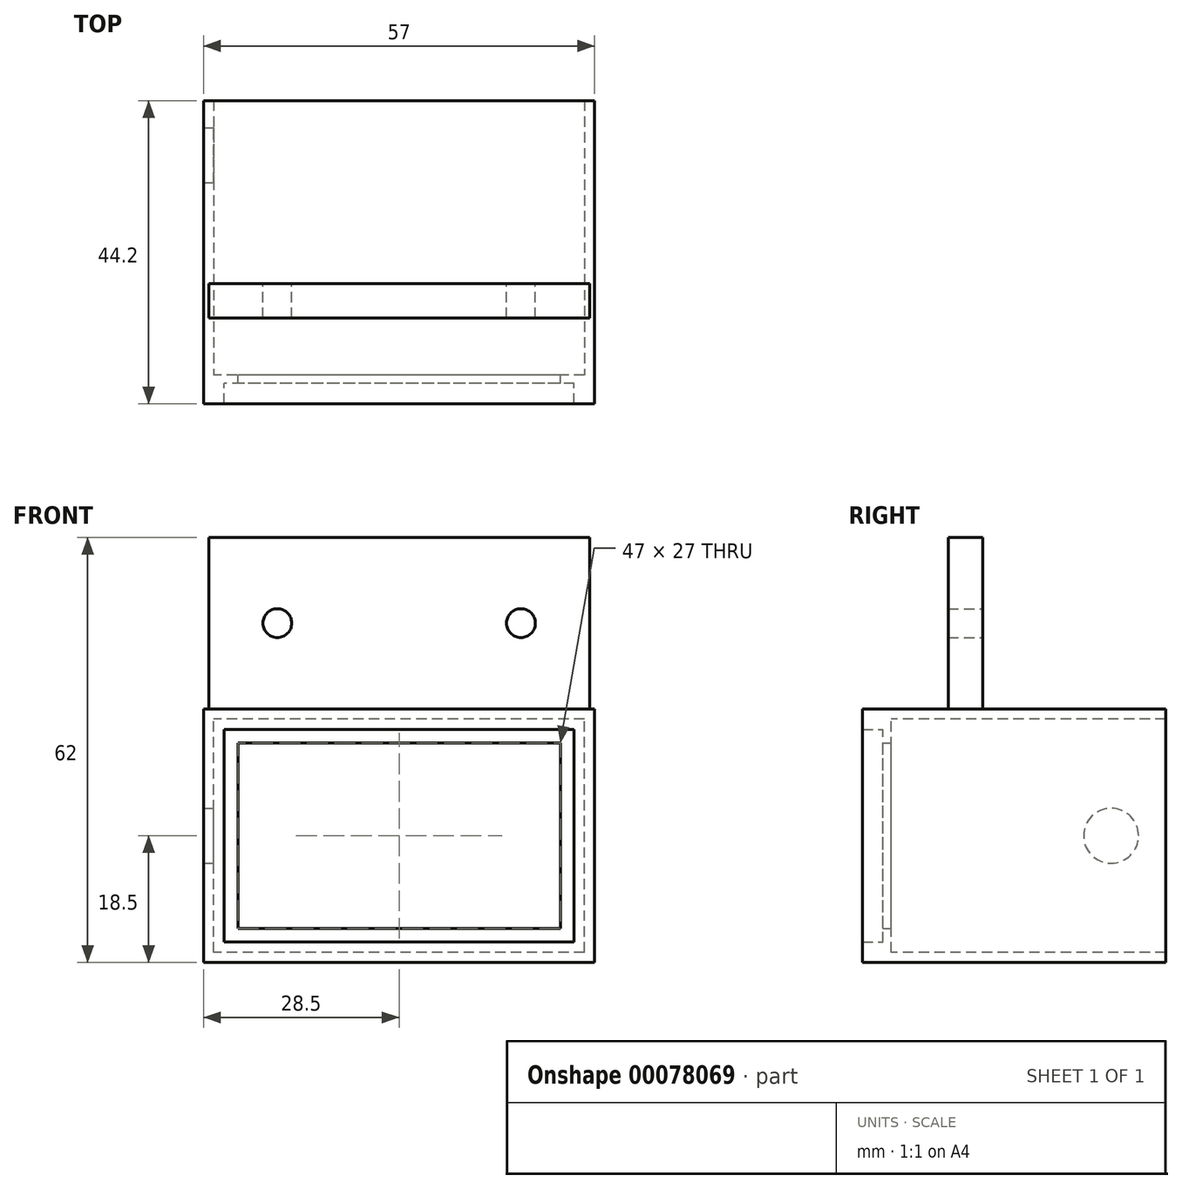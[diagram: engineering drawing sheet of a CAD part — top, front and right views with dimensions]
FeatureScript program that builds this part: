
annotation { "Feature Type Name" : "Feature", "Feature Type Description" : "" }
export const myFeature = defineFeature(function(context is Context, id is Id, definition is map)
    precondition{}
    {
        {
            var Q0;
            Q0=qCreatedBy(makeId("Front.planeOp"),FACE);
            var sketch = newSketch(context, id + "F0", { "sketchPlane" : qUnion([Q0])});
            skLineSegment(sketch, "E0.bottom", {"start": v(23.5, -13.5) * mm, "end": v(-23.5, -13.5) * mm});
            skLineSegment(sketch, "E0.top", {"start": v(23.5, 13.5) * mm, "end": v(-23.5, 13.5) * mm});
            skLineSegment(sketch, "E0.left", {"start": v(23.5, -13.5) * mm, "end": v(23.5, 13.5) * mm});
            skLineSegment(sketch, "E0.right", {"start": v(-23.5, -13.5) * mm, "end": v(-23.5, 13.5) * mm});
            skPoint(sketch, "E0.middle", {"position": v(0, 0) * mm});
            skLineSegment(sketch, "E1.0", {"start": v(-28.5, -18.5) * mm, "end": v(-28.5, 18.5) * mm});
            skLineSegment(sketch, "E1.1", {"start": v(28.5, -18.5) * mm, "end": v(-28.5, -18.5) * mm});
            skLineSegment(sketch, "E1.2", {"start": v(28.5, -18.5) * mm, "end": v(28.5, 18.5) * mm});
            skLineSegment(sketch, "E1.3", {"start": v(28.5, 18.5) * mm, "end": v(-28.5, 18.5) * mm});
            skSolve(sketch);
        }
        {
            var Q0;
            Q0=makeQuery(id+"F0.imprint","IMPRINT",FACE,{"disambiguationData":[TD([[makeQuery(id+"F0.imprint","IMPRINT",EDGE,{"derivedFrom":sQuery(id+"F0.wireOp",EDGE,"E0.bottom")}),1.0]])]});
            extrude(context, id + "F1", {"entities" : qUnion([Q0]), "depth" : 1.2 * mm, "offsetDistance" : 25 * mm});
        }
        {
            var Q0;
            Q0=makeQuery(id+"F1.opExtrude","CAP_FACE",FACE,{"disambiguationData":[OSD([sQuery(id+"F0.wireOp",EDGE,"E0.bottom"),sQuery(id+"F0.wireOp",EDGE,"E0.top"),sQuery(id+"F0.wireOp",EDGE,"E0.left"),sQuery(id+"F0.wireOp",EDGE,"E0.right"),sQuery(id+"F0.wireOp",EDGE,"E1.0"),sQuery(id+"F0.wireOp",EDGE,"E1.1"),sQuery(id+"F0.wireOp",EDGE,"E1.2"),sQuery(id+"F0.wireOp",EDGE,"E1.3")])],"isStart":false});
            var sketch = newSketch(context, id + "F2", { "sketchPlane" : qUnion([Q0])});
            skLineSegment(sketch, "E2.0", {"start": v(-25.5, -15.5) * mm, "end": v(-25.5, 15.5) * mm});
            skLineSegment(sketch, "E2.1", {"start": v(25.5, -15.5) * mm, "end": v(-25.5, -15.5) * mm});
            skLineSegment(sketch, "E2.2", {"start": v(25.5, -15.5) * mm, "end": v(25.5, 15.5) * mm});
            skLineSegment(sketch, "E2.3", {"start": v(25.5, 15.5) * mm, "end": v(-25.5, 15.5) * mm});
            skLineSegment(sketch, "E3.0", {"start": v(28.5, 18.5) * mm, "end": v(-28.5, 18.5) * mm});
            skLineSegment(sketch, "E3.1", {"start": v(28.5, -18.5) * mm, "end": v(28.5, 18.5) * mm});
            skLineSegment(sketch, "E3.2", {"start": v(28.5, -18.5) * mm, "end": v(-28.5, -18.5) * mm});
            skLineSegment(sketch, "E3.3", {"start": v(-28.5, -18.5) * mm, "end": v(-28.5, 18.5) * mm});
            skSolve(sketch);
        }
        {
            var Q0;
            Q0=makeQuery(id+"F2.imprint","IMPRINT",FACE,{"disambiguationData":[TD([[makeQuery(id+"F2.imprint","IMPRINT",EDGE,{"derivedFrom":sQuery(id+"F2.wireOp",EDGE,"E2.0")}),1.0]])]});
            extrude(context, id + "F3", {"entities" : qUnion([Q0]), "operationType" : NewBodyOperationType.ADD, "depth" : 3 * mm, "offsetDistance" : 25 * mm});
        }
        {
            var Q0;
            Q0=makeQuery(id+"F1.opExtrude","CAP_FACE",FACE,{"disambiguationData":[OSD([sQuery(id+"F0.wireOp",EDGE,"E0.bottom"),sQuery(id+"F0.wireOp",EDGE,"E0.top"),sQuery(id+"F0.wireOp",EDGE,"E0.left"),sQuery(id+"F0.wireOp",EDGE,"E0.right"),sQuery(id+"F0.wireOp",EDGE,"E1.0"),sQuery(id+"F0.wireOp",EDGE,"E1.1"),sQuery(id+"F0.wireOp",EDGE,"E1.2"),sQuery(id+"F0.wireOp",EDGE,"E1.3")])],"isStart":true});
            var sketch = newSketch(context, id + "F4", { "sketchPlane" : qUnion([Q0])});
            skLineSegment(sketch, "E4.0", {"start": v(-28.5, -18.5) * mm, "end": v(28.5, -18.5) * mm});
            skLineSegment(sketch, "E4.1", {"start": v(-28.5, -18.5) * mm, "end": v(-28.5, 18.5) * mm});
            skLineSegment(sketch, "E4.2", {"start": v(-28.5, 18.5) * mm, "end": v(28.5, 18.5) * mm});
            skLineSegment(sketch, "E4.3", {"start": v(28.5, -18.5) * mm, "end": v(28.5, 18.5) * mm});
            skLineSegment(sketch, "E5.0", {"start": v(-27, -17) * mm, "end": v(27, -17) * mm});
            skLineSegment(sketch, "E5.1", {"start": v(-27, -17) * mm, "end": v(-27, 17) * mm});
            skLineSegment(sketch, "E5.2", {"start": v(-27, 17) * mm, "end": v(27, 17) * mm});
            skLineSegment(sketch, "E5.3", {"start": v(27, -17) * mm, "end": v(27, 17) * mm});
            skSolve(sketch);
        }
        {
            var Q0;
            Q0=makeQuery(id+"F4.imprint","IMPRINT",FACE,{"disambiguationData":[TD([[makeQuery(id+"F4.imprint","IMPRINT",EDGE,{"derivedFrom":sQuery(id+"F4.wireOp",EDGE,"E4.0")}),1.0]])]});
            extrude(context, id + "F5", {"entities" : qUnion([Q0]), "operationType" : NewBodyOperationType.ADD, "depth" : 40 * mm, "offsetDistance" : 25 * mm});
        }
        {
            var Q0;
            Q0=makeQuery(id+"F5.boolean.opBoolean","MERGE",FACE,{"derivedFrom":[makeQuery(id+"F3.boolean.opBoolean","MERGE",FACE,{"derivedFrom":[makeQuery(id+"F1.opExtrude","SWEPT_FACE",FACE,{"disambiguationData":[OSD([sQuery(id+"F0.wireOp",EDGE,"E1.3")])]}),makeQuery(id+"F3.opExtrude","SWEPT_FACE",FACE,{"disambiguationData":[OSD([sQuery(id+"F2.wireOp",EDGE,"E3.0")])]})]}),makeQuery(id+"F5.opExtrude","SWEPT_FACE",FACE,{"disambiguationData":[OSD([sQuery(id+"F4.wireOp",EDGE,"E4.2")])]})]});
            var sketch = newSketch(context, id + "F6", { "sketchPlane" : qUnion([Q0])});
            skLineSegment(sketch, "E6.0", {"start": v(27.75, 8.3) * mm, "end": v(-27.75, 8.3) * mm});
            skLineSegment(sketch, "E7.0", {"start": v(27.75, 13.3) * mm, "end": v(-27.75, 13.3) * mm});
            skLineSegment(sketch, "E8", {"start": v(-27.75, 8.3) * mm, "end": v(-27.75, 13.3) * mm});
            skLineSegment(sketch, "E9", {"start": v(27.75, 13.3) * mm, "end": v(27.75, 8.3) * mm});
            skSolve(sketch);
        }
        {
            var Q0;
            Q0=makeQuery(id+"F6.imprint","IMPRINT",FACE,{"disambiguationData":[TD([[makeQuery(id+"F6.imprint","IMPRINT",EDGE,{"derivedFrom":sQuery(id+"F6.wireOp",EDGE,"E6.0")}),-1.0]])]});
            extrude(context, id + "F7", {"entities" : qUnion([Q0]), "operationType" : NewBodyOperationType.ADD, "depth" : 25 * mm, "offsetDistance" : 25 * mm});
        }
        {
            var Q0;
            Q0=makeQuery(id+"F7.opExtrude","SWEPT_FACE",FACE,{"disambiguationData":[OSD([sQuery(id+"F6.wireOp",EDGE,"E6.0")])]});
            var sketch = newSketch(context, id + "F8", { "sketchPlane" : qUnion([Q0])});
            skPoint(sketch, "E10", {"position": v(-17.75, 31) * mm});
            skPoint(sketch, "E11.MirrorP", {"position": v(17.75, 31) * mm});
            skSolve(sketch);
        }
        {
            var Q0;
            Q0=sQuery(id+"F8.wireOp",VERTEX,"E10");
            var Q1;
            Q1=sQuery(id+"F8.wireOp",VERTEX,"E11.MirrorP");
            var Q2;
            Q2=makeQuery(id+"F1.opExtrude","SWEPT_BODY",BODY,{"disambiguationData":[OSD([sQuery(id+"F0.wireOp",EDGE,"E0.bottom"),sQuery(id+"F0.wireOp",EDGE,"E0.top"),sQuery(id+"F0.wireOp",EDGE,"E0.left"),sQuery(id+"F0.wireOp",EDGE,"E0.right"),sQuery(id+"F0.wireOp",EDGE,"E1.0"),sQuery(id+"F0.wireOp",EDGE,"E1.1"),sQuery(id+"F0.wireOp",EDGE,"E1.2"),sQuery(id+"F0.wireOp",EDGE,"E1.3")])]});
            hole(context, id + "F9", {"style" : HoleStyle.SIMPLE, "endStyle" : HoleEndStyle.THROUGH, "holeDiameter" : 4.2 * mm, "majorDiameter" : 5 * mm, "tappedDepth" : 12 * mm, "tapClearance" : 3, "locations" : qUnion([Q0, Q1]), "scope" : qUnion([Q2])});
        }
        {
            var Q0;
            Q0=makeQuery(id+"F7.boolean.opBoolean","MERGE",FACE,{"derivedFrom":[makeQuery(id+"F5.boolean.opBoolean","MERGE",FACE,{"derivedFrom":[makeQuery(id+"F3.boolean.opBoolean","MERGE",FACE,{"derivedFrom":[makeQuery(id+"F1.opExtrude","SWEPT_FACE",FACE,{"disambiguationData":[OSD([sQuery(id+"F0.wireOp",EDGE,"E1.0")])]}),makeQuery(id+"F3.opExtrude","SWEPT_FACE",FACE,{"disambiguationData":[OSD([sQuery(id+"F2.wireOp",EDGE,"E3.3")])]})]}),makeQuery(id+"F5.opExtrude","SWEPT_FACE",FACE,{"disambiguationData":[OSD([sQuery(id+"F4.wireOp",EDGE,"E4.3")])]})]}),makeQuery(id+"F7.opExtrude","SWEPT_FACE",FACE,{"disambiguationData":[OSD([sQuery(id+"F6.wireOp",EDGE,"E8")])]})]});
            var sketch = newSketch(context, id + "F10", { "sketchPlane" : qUnion([Q0])});
            skPoint(sketch, "E12", {"position": v(-32.03, 0) * mm});
            skSolve(sketch);
        }
        {
            var Q0;
            Q0=sQuery(id+"F10.wireOp",VERTEX,"E12");
            var Q1;
            Q1=makeQuery(id+"F1.opExtrude","SWEPT_BODY",BODY,{"disambiguationData":[OSD([sQuery(id+"F0.wireOp",EDGE,"E0.bottom"),sQuery(id+"F0.wireOp",EDGE,"E0.top"),sQuery(id+"F0.wireOp",EDGE,"E0.left"),sQuery(id+"F0.wireOp",EDGE,"E0.right"),sQuery(id+"F0.wireOp",EDGE,"E1.0"),sQuery(id+"F0.wireOp",EDGE,"E1.1"),sQuery(id+"F0.wireOp",EDGE,"E1.2"),sQuery(id+"F0.wireOp",EDGE,"E1.3")])]});
            hole(context, id + "F11", {"style" : HoleStyle.SIMPLE, "endStyle" : HoleEndStyle.BLIND, "holeDiameter" : 8 * mm, "majorDiameter" : 5 * mm, "holeDepth" : 5 * mm, "tappedDepth" : 12 * mm, "tapClearance" : 3, "locations" : qUnion([Q0]), "scope" : qUnion([Q1])});
        }
    });
